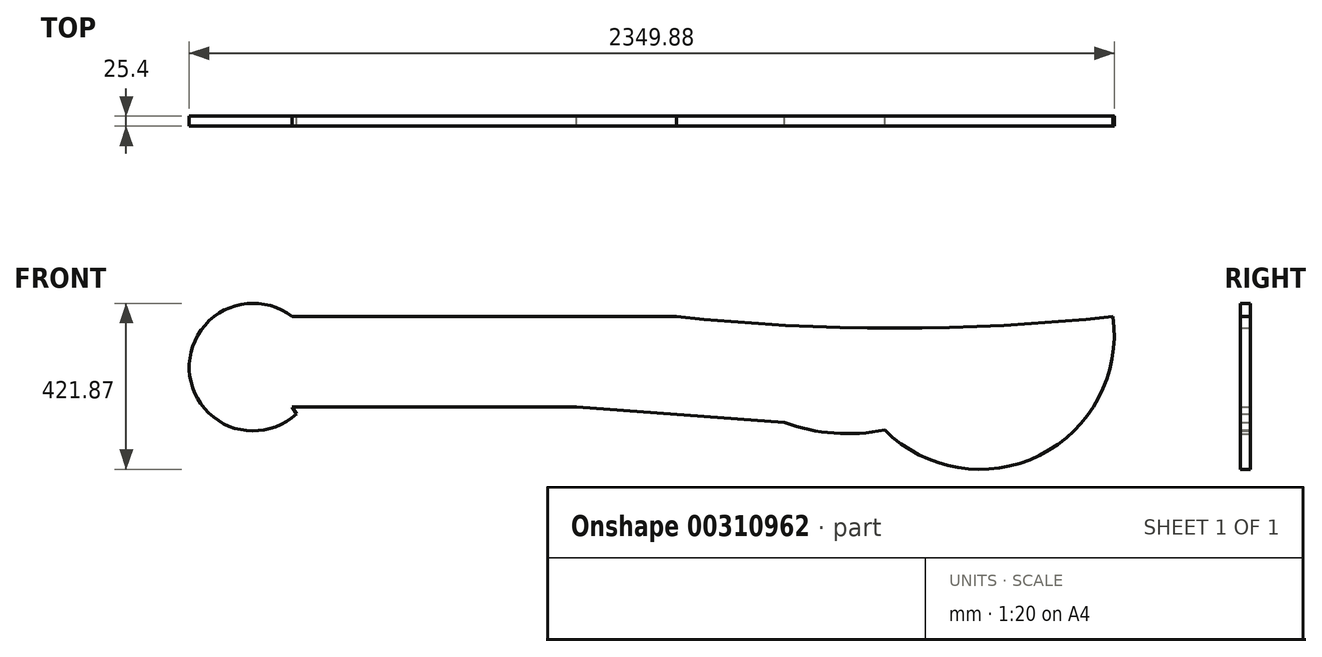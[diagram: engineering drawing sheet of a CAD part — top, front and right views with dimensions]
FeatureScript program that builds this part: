
annotation { "Feature Type Name" : "Feature", "Feature Type Description" : "" }
export const myFeature = defineFeature(function(context is Context, id is Id, definition is map)
    precondition{}
    {
        {
            var Q0;
            Q0=qCreatedBy(makeId("Front.planeOp"),FACE);
            var sketch = newSketch(context, id + "F0", { "sketchPlane" : qUnion([Q0])});
            skArc(sketch, "E0", {"start": v(-579.94, -287.77) * mm, "mid": v(-186.62, -352.17) * mm, "end": v(0, 0) * mm});
            skArc(sketch, "E1", {"start": v(-579.94, -287.77) * mm, "mid": v(-836.98, -130.33) * mm, "end": v(-1108.77, 0) * mm});
            skArc(sketch, "E2", {"start": v(-1108.77, 0) * mm, "mid": v(-554.38, -29.04) * mm, "end": v(0, 0) * mm});
            skArc(sketch, "E3", {"start": v(-1108.77, 0) * mm, "mid": v(-896.9, -240.44) * mm, "end": v(-579.94, -287.77) * mm});
            skArc(sketch, "E4", {"start": v(-1581.5, 0) * mm, "mid": v(-1345.13, -229.45) * mm, "end": v(-1108.77, 0) * mm});
            skLineSegment(sketch, "E5", {"start": v(-1581.5, 0) * mm, "end": v(-1108.77, 0) * mm});
            skLineSegment(sketch, "E6", {"start": v(-579.94, -287.77) * mm, "end": v(-1362.9, -228.78) * mm});
            skLineSegment(sketch, "E7", {"start": v(-1362.9, -228.78) * mm, "end": v(-1581.5, 0) * mm});
            skLineSegment(sketch, "E8", {"start": v(-1581.5, 0) * mm, "end": v(-2085.14, 0) * mm});
            skLineSegment(sketch, "E9", {"start": v(-2085.14, 0) * mm, "end": v(-1362.9, -228.78) * mm});
            skLineSegment(sketch, "E10", {"start": v(-2085.14, 0) * mm, "end": v(-2085.14, -228.78) * mm});
            skLineSegment(sketch, "E11", {"start": v(-2085.14, -228.78) * mm, "end": v(-1362.9, -228.78) * mm});
            skArc(sketch, "E12", {"start": v(-2085.14, 0) * mm, "mid": v(-2346.59, -135.07) * mm, "end": v(-2074.4, -246.95) * mm});
            skLineSegment(sketch, "E13", {"start": v(-2085.14, -228.78) * mm, "end": v(-2074.4, -246.95) * mm});
            skSolve(sketch);
        }
        {
            var Q0;
            Q0 = qSketchRegion(id + "F0", true);
            extrude(context, id + "F1", {"entities" : qUnion([Q0]), "depth" : 25.4 * mm});
        }
    });
